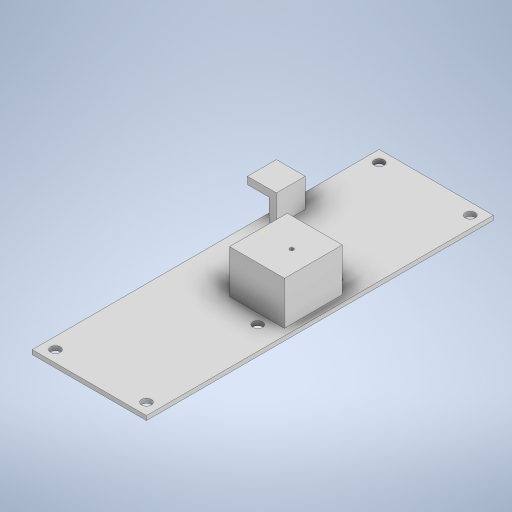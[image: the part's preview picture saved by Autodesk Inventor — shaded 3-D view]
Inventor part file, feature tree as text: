
AUTODESK INVENTOR PART (.ipt)
format: ipt  version: 2023 (Build 270158000, 158)  size: 342,528 bytes
history: native  units: mm
features: sketch x13, extrude x12
ambient origin geometry x8: Origin, YZ Plane, XZ Plane, XY Plane, X Axis, Y Axis, Z Axis, Center Point
bodies: Body1 (feature_tree)
feature tree (25):
  extrude  "Extrusion33"  Depth=240.0mm
  extrude  "Extrusion34"  Depth=38.0mm
  extrude  "Extrusion35"  Depth=30.0mm TaperAngle=0.0deg
  extrude  "Extrusion38"  Depth=30.0mm
  extrude  "Extrusion39"  Depth=15.0mm
  extrude  "Extrusion40"  Depth=3.5mm
  extrude  "Extrusion41"  Depth=35.0mm TaperAngle=0.0deg
  extrude  "Extrusion43"  Depth=20.0mm
  extrude  "Extrusion46"  Depth=20.0mm
  extrude  "Extrusion47"  Depth=5.0mm TaperAngle=0.0deg
  extrude  "Extrusion48"  Depth=10.0mm TaperAngle=0.0deg
  sketch  "Sketch71"  dims[d192=6.7mm d193=6.7mm]
  extrude  "Extrusion49"  Depth=6.7mm
  sketch  "Sketch44"  dims[d138=79.0mm d139=240.0mm]
  sketch  "Sketch45"  dims[d140=3.0mm d141=0.0mm d142=38.0mm]
  sketch  "Sketch47"  dims[d143=40.0mm d144=30.0mm d145=0.0mm]
  sketch  "Sketch58"  dims[d146=36.0mm d147=30.0mm d148=-2.617994mm]
  sketch  "Sketch59"  dims[d156=20.0mm d157=15.0mm]
  sketch  "Sketch60"  dims[d158=15.0mm d159=0.0mm d160=3.5mm]
  sketch  "Sketch61"  dims[d161=20.0mm d162=35.0mm d163=0.0mm]
  sketch  "Sketch65"  dims[d164=5.0mm d165=20.0mm]
  sketch  "Sketch68"  dims[d166=20.0mm d167=0.0mm d168=20.0mm]
  sketch  "Sketch69"  dims[d169=20.0mm d170=5.0mm d171=0.0mm]
  sketch  "Sketch70"  dims[d176=6.0mm d177=10.0mm d178=0.0mm]
  sketch  "Sketch72"  dims[d194=6.7mm d195=6.7mm d196=10.0mm d197=0.0mm d198=6.7mm d199=6.7mm d200=10.0mm d201=0.0mm d202=8.0mm d203=0.0mm d204=2.5mm d205=10.0mm d206=0.0mm d49=0.5mm d50=0.872665mm d51=0.5mm d52=0.872665mm d130=0.5mm d131=0.872665mm d132=0.5mm d133=0.872665mm d173=0.5mm d174=0.872665mm d175=0.5mm]
